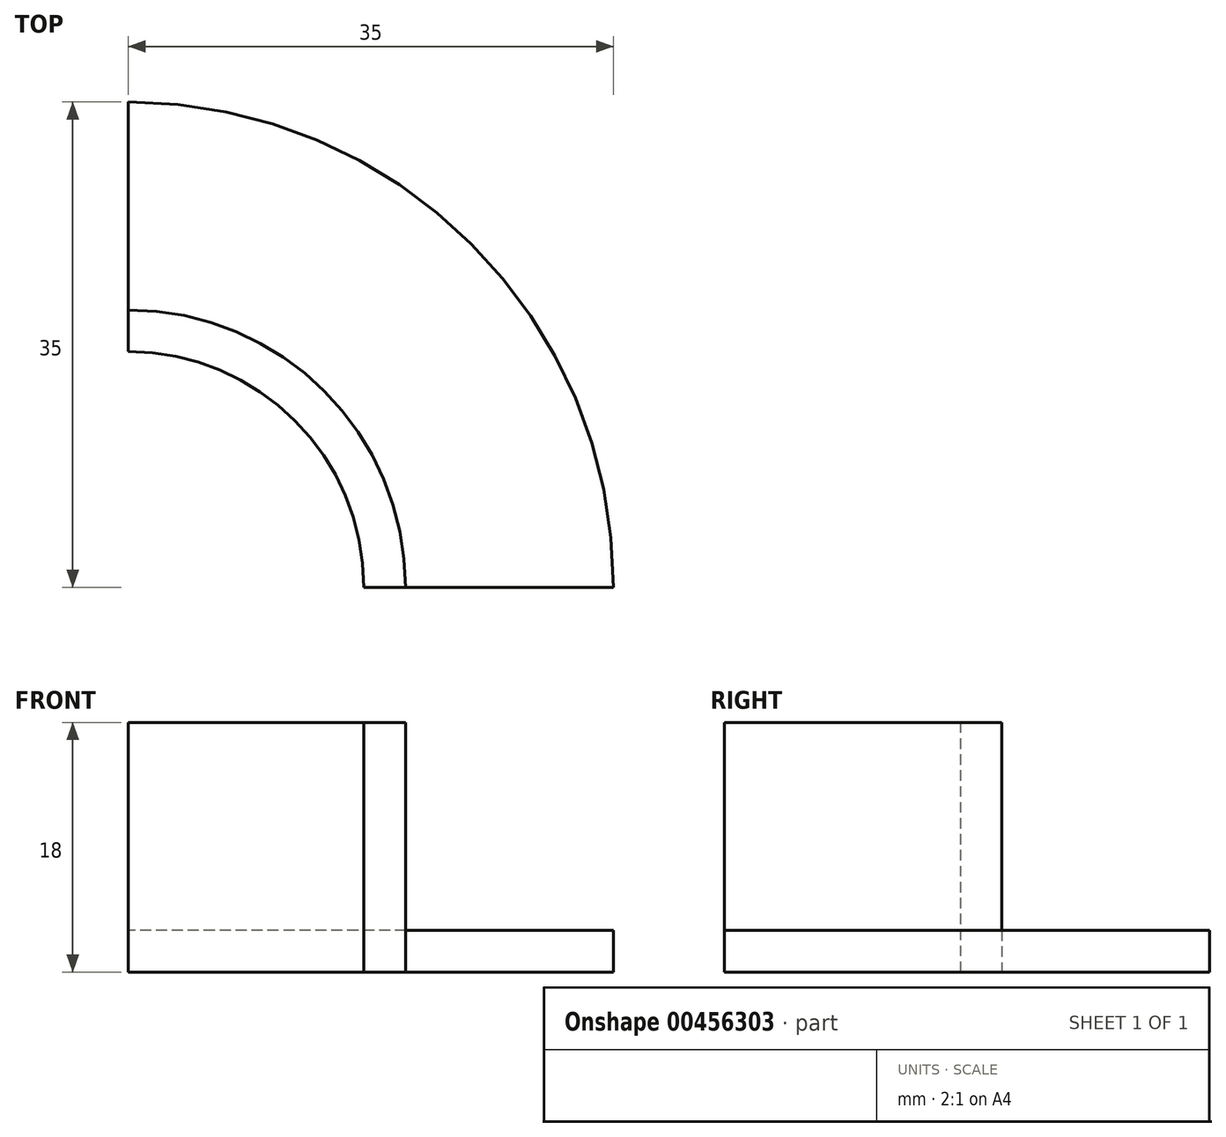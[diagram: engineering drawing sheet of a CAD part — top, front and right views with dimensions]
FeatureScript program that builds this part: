
annotation { "Feature Type Name" : "Feature", "Feature Type Description" : "" }
export const myFeature = defineFeature(function(context is Context, id is Id, definition is map)
    precondition{}
    {
        {
            var Q0;
            Q0=qCreatedBy(makeId("Top.planeOp"),FACE);
            var sketch = newSketch(context, id + "F0", { "sketchPlane" : qUnion([Q0])});
            skCircle(sketch, "E0", {"center": v(0, 0) * mm, "radius": 35 * mm});
            skCircle(sketch, "E1", {"center": v(0, 0) * mm, "radius": 20 * mm});
            skCircle(sketch, "E2", {"center": v(0, 0) * mm, "radius": 17 * mm});
            skLineSegment(sketch, "E3", {"start": v(0, 35) * mm, "end": v(0, 17) * mm});
            skLineSegment(sketch, "E4", {"start": v(17, 0) * mm, "end": v(35, 0) * mm});
            skSolve(sketch);
        }
        {
            var Q0;
            Q0=qCreatedBy(makeId("Top.planeOp"),FACE);
            var sketch = newSketch(context, id + "F1", { "sketchPlane" : qUnion([Q0])});
            skCircle(sketch, "E5", {"center": v(0, 0) * mm, "radius": 35 * mm});
            skCircle(sketch, "E6", {"center": v(0, 0) * mm, "radius": 20 * mm});
            skCircle(sketch, "E7", {"center": v(0, 0) * mm, "radius": 17 * mm});
            skLineSegment(sketch, "E8", {"start": v(0, 35) * mm, "end": v(0, 17) * mm});
            skLineSegment(sketch, "E9", {"start": v(17, 0) * mm, "end": v(35, 0) * mm});
            skSolve(sketch);
        }
        {
            var Q0;
            {var subQ0=sQuery(id+"F0.wireOp",EDGE,"E3");var subQ1=sQuery(id+"F0.wireOp",EDGE,"E0");var subQ2=makeQuery(id+"F0.imprint","INTERSECT",VERTEX,{"derivedFrom":[subQ1,subQ0]});Q0=makeQuery(id+"F0.imprint","IMPRINT",FACE,{"disambiguationData":[TD([[makeQuery(id+"F0.imprint","IMPRINT",EDGE,{"disambiguationData":[TD([[subQ2,1.0]])],"derivedFrom":subQ1}),1.0]])]});}
            extrude(context, id + "F2", {"entities" : qUnion([Q0]), "depth" : 3 * mm});
        }
        {
            var Q0;
            {var subQ0=sQuery(id+"F0.wireOp",EDGE,"E3");var subQ1=sQuery(id+"F0.wireOp",EDGE,"E1");var subQ2=makeQuery(id+"F0.imprint","INTERSECT",VERTEX,{"derivedFrom":[subQ1,subQ0]});Q0=makeQuery(id+"F0.imprint","IMPRINT",FACE,{"disambiguationData":[TD([[makeQuery(id+"F0.imprint","IMPRINT",EDGE,{"disambiguationData":[TD([[subQ2,1.0]])],"derivedFrom":subQ1}),1.0]])]});}
            extrude(context, id + "F3", {"entities" : qUnion([Q0]), "operationType" : NewBodyOperationType.ADD, "depth" : 18 * mm});
        }
        {
            var Q0;
            {var subQ0=sQuery(id+"F1.wireOp",EDGE,"E8");var subQ1=sQuery(id+"F1.wireOp",EDGE,"E5");var subQ2=makeQuery(id+"F1.imprint","INTERSECT",VERTEX,{"derivedFrom":[subQ1,subQ0]});Q0=makeQuery(id+"F1.imprint","IMPRINT",FACE,{"disambiguationData":[TD([[makeQuery(id+"F1.imprint","IMPRINT",EDGE,{"disambiguationData":[TD([[subQ2,1.0]])],"derivedFrom":subQ1}),1.0]])]});}
            extrude(context, id + "F4", {"entities" : qUnion([Q0]), "depth" : 3 * mm});
        }
    });
